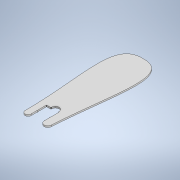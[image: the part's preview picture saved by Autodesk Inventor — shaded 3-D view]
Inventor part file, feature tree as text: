
AUTODESK INVENTOR PART (.ipt)
format: ipt  version: 2021 (Build 250183000, 183)  size: 177,152 bytes
history: native  units: in
note: dims shown in document units (in); Inventor stores cm internally (conversion verified against a paired STEP export)
features: extrude x1, fillet x1, sketch x1
ambient origin geometry x8: Origin, YZ Plane, XZ Plane, XY Plane, X Axis, Y Axis, Z Axis, Center Point
bodies: Solid1 (feature_tree)
feature tree (3):
  extrude  "Extrusion1"  Depth=0.125in
  fillet  "Fillet1"  Radius=1.5in
  sketch  "Sketch2"  dims[d19=5.5in d20=12.5in d24=1.5in d31=0.5in d32=0.0in d35=2.0in d37=9.5in d51=0.25in d52=2.0in d60=180.0deg d61=4.5in d76=180.0deg d81=0.25in d82=90.0deg d83=0.125in d84=2.0in d85=2.75in d86=1.5in d98=2.5in d99=180.0deg d100=1.25in d101=90.0deg d102=3.0in d103=0.125in]
